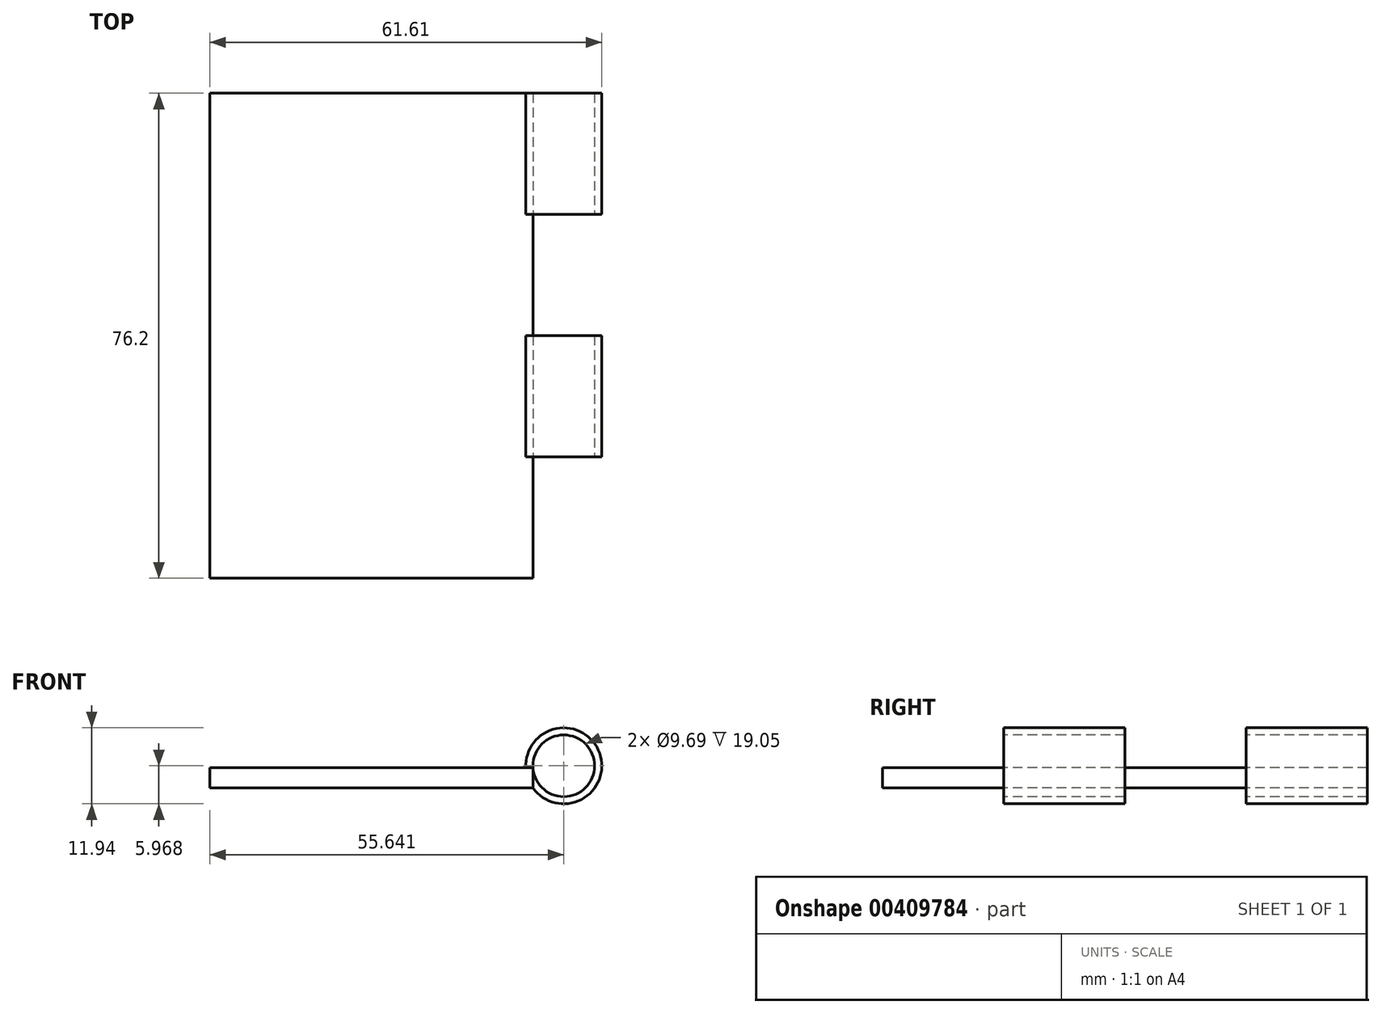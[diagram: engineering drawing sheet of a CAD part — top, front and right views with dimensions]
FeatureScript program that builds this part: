
annotation { "Feature Type Name" : "Feature", "Feature Type Description" : "" }
export const myFeature = defineFeature(function(context is Context, id is Id, definition is map)
    precondition{}
    {
        {
            var Q0;
            Q0=qCreatedBy(makeId("Top.planeOp"),FACE);
            var sketch = newSketch(context, id + "F0", { "sketchPlane" : qUnion([Q0])});
            skLineSegment(sketch, "E0.bottom", {"start": v(-23.9, 0) * mm, "end": v(26.9, 0) * mm});
            skLineSegment(sketch, "E0.top", {"start": v(-23.9, -76.2) * mm, "end": v(26.9, -76.2) * mm});
            skLineSegment(sketch, "E0.left", {"start": v(-23.9, 0) * mm, "end": v(-23.9, -76.2) * mm});
            skLineSegment(sketch, "E0.right", {"start": v(26.9, 0) * mm, "end": v(26.9, -76.2) * mm});
            skSolve(sketch);
        }
        {
            var Q0;
            Q0=makeQuery(id+"F0.imprint","IMPRINT",FACE,{"disambiguationData":[TD([[makeQuery(id+"F0.imprint","IMPRINT",EDGE,{"derivedFrom":sQuery(id+"F0.wireOp",EDGE,"E0.bottom")}),-1.0]])]});
            extrude(context, id + "F1", {"entities" : qUnion([Q0]), "depth" : 3.17 * mm});
        }
        {
            var Q0;
            Q0=qCreatedBy(makeId("Front.planeOp"),FACE);
            var sketch = newSketch(context, id + "F2", { "sketchPlane" : qUnion([Q0])});
            skCircle(sketch, "E1", {"center": v(31.73, 3.5) * mm, "radius": 4.76 * mm});
            skPoint(sketch, "E1.first.point", {"position": v(20.1, 0) * mm});
            skPoint(sketch, "E1.second.point", {"position": v(28.09, 3.5) * mm});
            skPoint(sketch, "E1.third.point", {"position": v(29.56, -0.75) * mm});
            skSolve(sketch);
        }
        {
            var Q0;
            Q0=makeQuery(id+"F1.opExtrude","SWEPT_FACE",FACE,{"disambiguationData":[OSD([sQuery(id+"F0.wireOp",EDGE,"E0.right")])]});
            var sketch = newSketch(context, id + "F3", { "sketchPlane" : qUnion([Q0])});
            skLineSegment(sketch, "E2", {"start": v(-38.1, 3.18) * mm, "end": v(-38.1, 0) * mm});
            skLineSegment(sketch, "E3", {"start": v(-38.1, 0) * mm, "end": v(-19.05, 0) * mm});
            skLineSegment(sketch, "E4", {"start": v(-19.05, 0) * mm, "end": v(-19.05, 3.18) * mm});
            skLineSegment(sketch, "E5", {"start": v(-19.05, 3.18) * mm, "end": v(-38.1, 3.18) * mm});
            skLineSegment(sketch, "E6", {"start": v(-38.1, 3.18) * mm, "end": v(-57.15, 3.18) * mm});
            skLineSegment(sketch, "E7", {"start": v(-57.15, 3.18) * mm, "end": v(-57.15, 0) * mm});
            skLineSegment(sketch, "E8", {"start": v(-57.15, 0) * mm, "end": v(-76.2, 0) * mm});
            skLineSegment(sketch, "E9", {"start": v(-19.05, 3.18) * mm, "end": v(0, 3.18) * mm});
            skSolve(sketch);
        }
        {
            var Q0;
            {var subQ0=sQuery(id+"F3.wireOp",EDGE,"E4");Q0=makeQuery(id+"F3.imprint","IMPRINT",FACE,{"disambiguationData":[TD([[makeQuery(id+"F3.imprint","IMPRINT",EDGE,{"derivedFrom":subQ0}),-1.0]])]});}
            var Q1;
            {var subQ0=sQuery(id+"F3.wireOp",EDGE,"E2");Q1=makeQuery(id+"F3.imprint","IMPRINT",FACE,{"disambiguationData":[TD([[makeQuery(id+"F3.imprint","IMPRINT",EDGE,{"derivedFrom":subQ0}),-1.0]])]});}
            var Q2;
            Q2=sQuery(id+"F2.wireOp",EDGE,"E1");
            sweep(context, id + "F4", {"operationType" : NewBodyOperationType.ADD, "profiles" : qUnion([Q0, Q1]), "path" : qUnion([Q2])});
        }
    });
